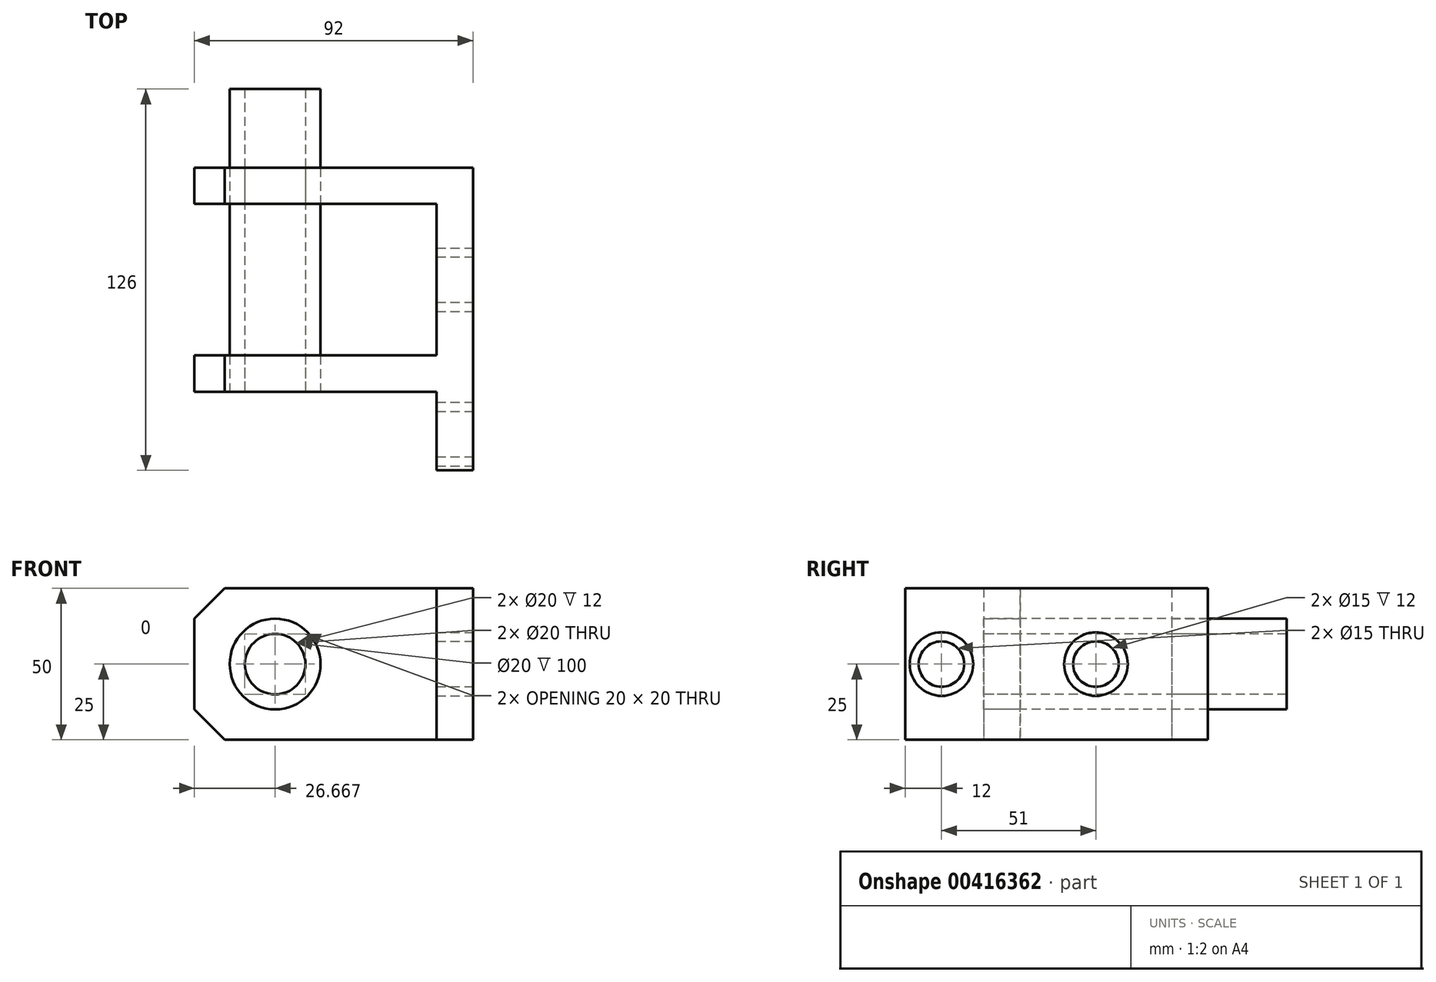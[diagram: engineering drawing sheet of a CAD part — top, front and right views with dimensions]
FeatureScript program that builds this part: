
annotation { "Feature Type Name" : "Feature", "Feature Type Description" : "" }
export const myFeature = defineFeature(function(context is Context, id is Id, definition is map)
    precondition{}
    {
        {
            assignVariable(context, id + "F0", {"name" : "length", "anyValue" : 100});
        }
        {
            assignVariable(context, id + "F1", {"name" : "thickness", "anyValue" : 12});
        }
        {
            var Q0;
            Q0=qCreatedBy(makeId("Top.planeOp"),FACE);
            var sketch = newSketch(context, id + "F2", { "sketchPlane" : qUnion([Q0])});
            skLineSegment(sketch, "E0", {"start": v(0, 0) * mm, "end": v(0, 100) * mm});
            skLineSegment(sketch, "E1", {"start": v(0, 100) * mm, "end": v(-12, 100) * mm});
            skLineSegment(sketch, "E2", {"start": v(-12, 100) * mm, "end": v(-12, 100) * mm});
            skLineSegment(sketch, "E3", {"start": v(-12, 100) * mm, "end": v(-92, 100) * mm});
            skLineSegment(sketch, "E4", {"start": v(-92, 100) * mm, "end": v(-92, 88) * mm});
            skLineSegment(sketch, "E5", {"start": v(-92, 88) * mm, "end": v(-12, 88) * mm});
            skLineSegment(sketch, "E6", {"start": v(-12, 88) * mm, "end": v(-12, 38) * mm});
            skLineSegment(sketch, "E7", {"start": v(-12, 38) * mm, "end": v(-92, 38) * mm});
            skLineSegment(sketch, "E8", {"start": v(-92, 38) * mm, "end": v(-92, 26) * mm});
            skLineSegment(sketch, "E9", {"start": v(-92, 26) * mm, "end": v(-12, 26) * mm});
            skLineSegment(sketch, "E10", {"start": v(-12, 26) * mm, "end": v(-12, 0) * mm});
            skLineSegment(sketch, "E11", {"start": v(-12, 0) * mm, "end": v(0, 0) * mm});
            skSolve(sketch);
        }
        {
            var Q0;
            Q0=makeQuery(id+"F2.imprint","IMPRINT",FACE,{"disambiguationData":[TD([[makeQuery(id+"F2.imprint","IMPRINT",EDGE,{"derivedFrom":sQuery(id+"F2.wireOp",EDGE,"E0")}),1.0]])]});
            extrude(context, id + "F3", {"entities" : qUnion([Q0]), "endBound" : BoundingType.SYMMETRIC, "depth" : 50 * mm});
        }
        {
            var Q0;
            Q0=qCreatedBy(makeId("Front.planeOp"),FACE);
            var sketch = newSketch(context, id + "F4", { "sketchPlane" : qUnion([Q0])});
            skLineSegment(sketch, "E12", {"start": v(-117, 60) * mm, "end": v(-117, -60) * mm});
            skLineSegment(sketch, "E13", {"start": v(-117, -60) * mm, "end": v(-47, -60) * mm});
            skLineSegment(sketch, "E14", {"start": v(-47, -60) * mm, "end": v(-107, 0) * mm});
            skLineSegment(sketch, "E15", {"start": v(-107, 0) * mm, "end": v(-47, 60) * mm});
            skLineSegment(sketch, "E16", {"start": v(-47, 60) * mm, "end": v(-117, 60) * mm});
            skSolve(sketch);
        }
        {
            var Q0;
            Q0=qSketchRegion(id+"F4",true);
            var Q1;
            Q1=qConstructionFilter(qBodyType(qCreatedBy(id+"F4",EDGE),BodyType.WIRE),ConstructionObject.NO);
            extrude(context, id + "F5", {"entities" : qUnion([Q0]), "operationType" : NewBodyOperationType.REMOVE, "surfaceEntities" : qUnion([Q1]), "oppositeDirection" : true, "depth" : 111.8 * mm});
        }
        {
            var Q0;
            Q0=qCreatedBy(makeId("Front.planeOp"),FACE);
            var sketch = newSketch(context, id + "F6", { "sketchPlane" : qUnion([Q0])});
            skCircle(sketch, "E17", {"center": v(-65.33, 0) * mm, "radius": 10 * mm});
            skSolve(sketch);
        }
        {
            var Q0;
            Q0=qSketchRegion(id+"F6",true);
            var Q1;
            Q1=sQuery(id+"F6.wireOp",EDGE,"E17");
            extrude(context, id + "F7", {"entities" : qUnion([Q0]), "operationType" : NewBodyOperationType.REMOVE, "surfaceEntities" : qUnion([Q1]), "oppositeDirection" : true, "depth" : 108 * mm});
        }
        {
            var Q0;
            Q0=qCreatedBy(makeId("Right.planeOp"),FACE);
            var sketch = newSketch(context, id + "F9", { "sketchPlane" : qUnion([Q0])});
            skLineSegment(sketch, "E18.direction1", {"start": v(63, 29) * mm, "end": v(10.5, 29) * mm, "construction": true});
            skCircle(sketch, "E19", {"center": v(63, 0) * mm, "radius": 7.5 * mm});
            skCircle(sketch, "E20", {"center": v(12, 0) * mm, "radius": 7.5 * mm});
            skSolve(sketch);
        }
        {
            var Q0;
            Q0=qSketchRegion(id+"F9",true);
            extrude(context, id + "F10", {"entities" : qUnion([Q0]), "operationType" : NewBodyOperationType.REMOVE, "oppositeDirection" : true, "depth" : 3 * (getVariable(context, 'thickness')) * mm});
        }
        {
            var Q0;
            Q0=makeQuery(id+"F3.opExtrude","SWEPT_FACE",FACE,{"disambiguationData":[OSD([sQuery(id+"F2.wireOp",EDGE,"E9")])]});
            var sketch = newSketch(context, id + "F11", { "sketchPlane" : qUnion([Q0])});
            skCircle(sketch, "E21", {"center": v(-65.33, 0) * mm, "radius": 10 * mm});
            skCircle(sketch, "E22", {"center": v(-65.33, 0) * mm, "radius": 15 * mm});
            skSolve(sketch);
        }
        {
            var Q0;
            Q0 = qSketchRegion(id + "F11", true);
            extrude(context, id + "F12", {"entities" : qUnion([Q0]), "oppositeDirection" : true, "depth" : (getVariable(context, 'length')) * mm});
        }
        {
            var Q0;
            Q0=makeQuery(id+"F12.opExtrude","SWEPT_BODY",BODY,{"disambiguationData":[OSD([sQuery(id+"F11.wireOp",EDGE,"E21"),sQuery(id+"F11.wireOp",EDGE,"E22")])]});
            var Q1;
            Q1=makeQuery(id+"F3.opExtrude","SWEPT_BODY",BODY,{"disambiguationData":[OSD([sQuery(id+"F2.wireOp",EDGE,"E0"),sQuery(id+"F2.wireOp",EDGE,"E1"),sQuery(id+"F2.wireOp",EDGE,"E3"),sQuery(id+"F2.wireOp",EDGE,"E4"),sQuery(id+"F2.wireOp",EDGE,"E5"),sQuery(id+"F2.wireOp",EDGE,"E6"),sQuery(id+"F2.wireOp",EDGE,"E7"),sQuery(id+"F2.wireOp",EDGE,"E8"),sQuery(id+"F2.wireOp",EDGE,"E9"),sQuery(id+"F2.wireOp",EDGE,"E10"),sQuery(id+"F2.wireOp",EDGE,"E11")])]});
            booleanBodies(context, id + "F13", {"operationType" : BooleanOperationType.INTERSECTION, "tools" : qUnion([Q0, Q1]), "keepTools" : true});
        }
        {
            var Q0;
            Q0=makeQuery(id+"F3.opExtrude","SWEPT_FACE",FACE,{"disambiguationData":[OSD([sQuery(id+"F2.wireOp",EDGE,"E0")])]});
            var sketch = newSketch(context, id + "F14", { "sketchPlane" : qUnion([Q0])});
            skCircle(sketch, "E23", {"center": v(12, 0) * mm, "radius": 7.5 * mm});
            skCircle(sketch, "E24", {"center": v(63, 0) * mm, "radius": 7.5 * mm});
            skCircle(sketch, "E25.0", {"center": v(12, 0) * mm, "radius": 10.5 * mm});
            skCircle(sketch, "E26.0", {"center": v(63, 0) * mm, "radius": 10.5 * mm});
            skSolve(sketch);
        }
        {
            var Q0;
            Q0 = qSketchRegion(id + "F14", true);
            extrude(context, id + "F15", {"entities" : qUnion([Q0]), "oppositeDirection" : true, "depth" : (getVariable(context, 'thickness')) * mm});
        }
    });
